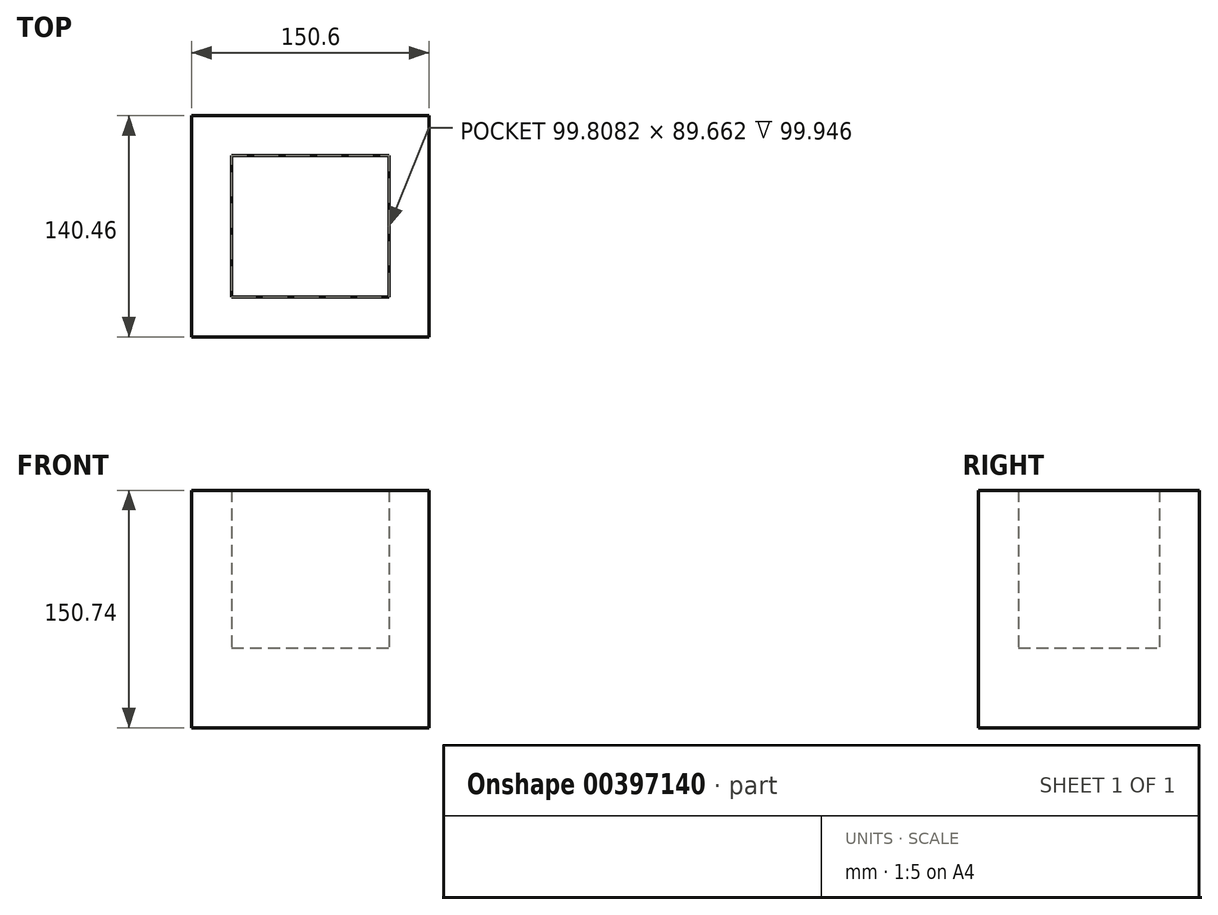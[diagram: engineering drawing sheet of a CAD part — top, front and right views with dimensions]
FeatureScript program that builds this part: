
annotation { "Feature Type Name" : "Feature", "Feature Type Description" : "" }
export const myFeature = defineFeature(function(context is Context, id is Id, definition is map)
    precondition{}
    {
        {
            var Q0;
            Q0=qCreatedBy(makeId("Front.planeOp"),FACE);
            var sketch = newSketch(context, id + "F0", { "sketchPlane" : qUnion([Q0])});
            skLineSegment(sketch, "E0.bottom", {"start": v(-75.3, 74.7) * mm, "end": v(75.3, 74.7) * mm});
            skLineSegment(sketch, "E0.top", {"start": v(-75.3, -76.05) * mm, "end": v(75.3, -76.05) * mm});
            skLineSegment(sketch, "E0.left", {"start": v(-75.3, 74.7) * mm, "end": v(-75.3, -76.05) * mm});
            skLineSegment(sketch, "E0.right", {"start": v(75.3, 74.7) * mm, "end": v(75.3, -76.05) * mm});
            skSolve(sketch);
        }
        {
            var Q0;
            Q0 = qSketchRegion(id + "F0", true);
            extrude(context, id + "F1", {"entities" : qUnion([Q0]), "depth" : 140.46 * mm});
        }
        {
            var Q0;
            Q0=makeQuery(id+"F1.opExtrude","SWEPT_FACE",FACE,{"disambiguationData":[OSD([sQuery(id+"F0.wireOp",EDGE,"E0.bottom")])]});
            shell(context, id + "F2", {"entities" : qUnion([Q0]), "thickness" : 25.4 * mm});
        }
        {
            var Q0;
            Q0=makeQuery(id+"F2.opShell","OFFSET_FACE",FACE,{"disambiguationData":[OSD([sQuery(id+"F0.wireOp",EDGE,"E0.top")])]});
            extrude(context, id + "F3", {"entities" : qUnion([Q0]), "operationType" : NewBodyOperationType.ADD, "depth" : 25.4 * mm});
        }
    });
